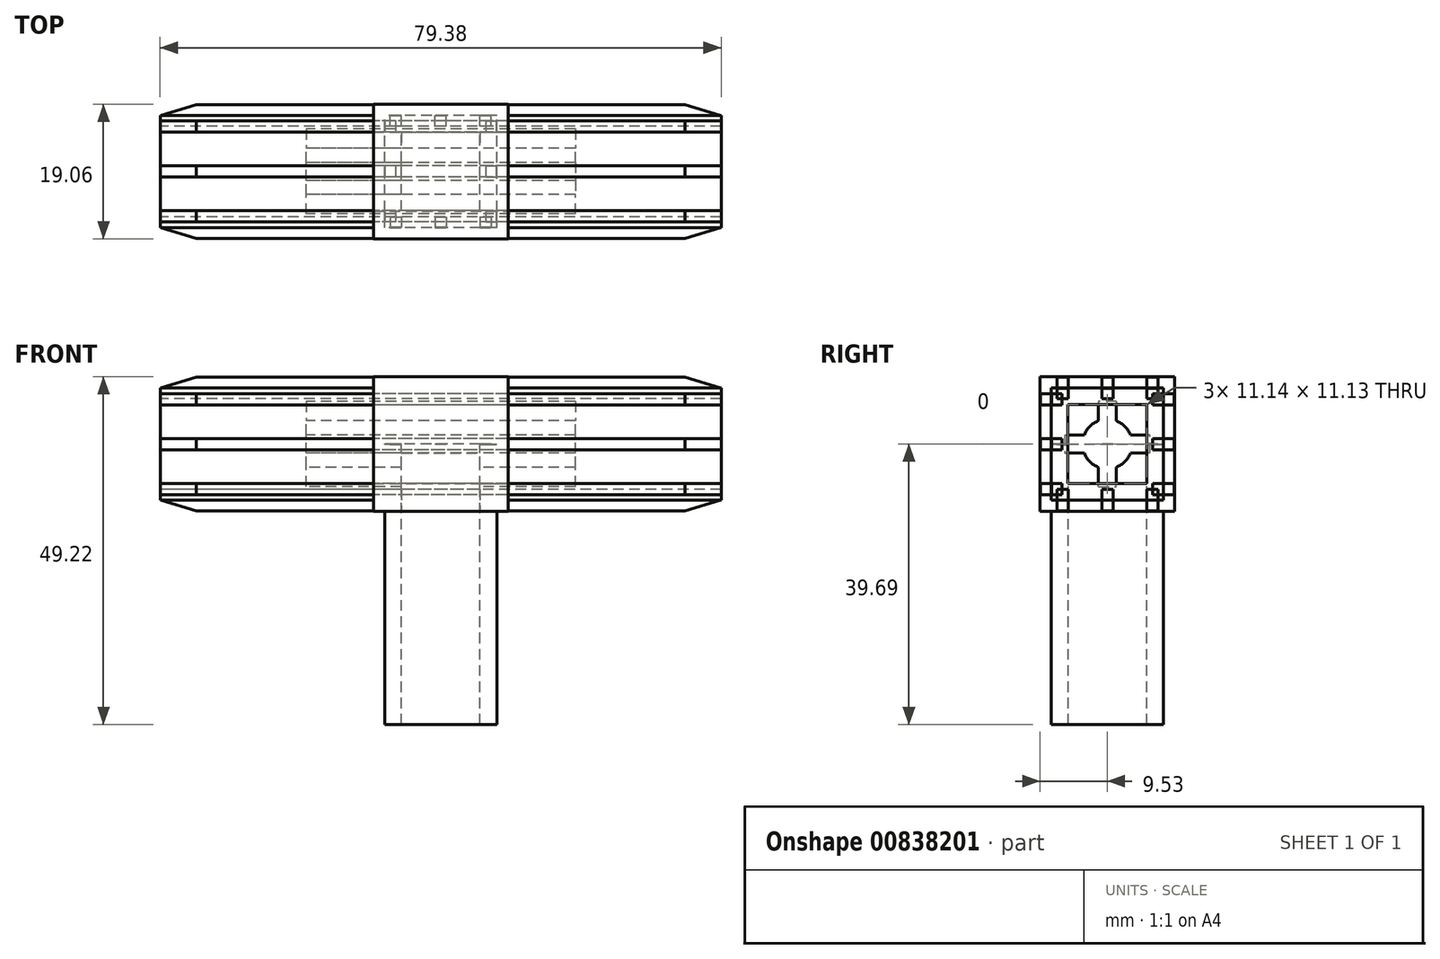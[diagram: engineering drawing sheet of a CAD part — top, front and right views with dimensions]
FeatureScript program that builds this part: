
annotation { "Feature Type Name" : "Feature", "Feature Type Description" : "" }
export const myFeature = defineFeature(function(context is Context, id is Id, definition is map)
    precondition{}
    {
        {
            var Q0;
            Q0=qCreatedBy(makeId("Top.planeOp"),FACE);
            var sketch = newSketch(context, id + "F0", { "sketchPlane" : qUnion([Q0])});
            skLineSegment(sketch, "E0.bottom", {"start": v(39.69, -7.94) * mm, "end": v(-39.69, -7.94) * mm});
            skLineSegment(sketch, "E0.top", {"start": v(39.69, 7.94) * mm, "end": v(-39.69, 7.94) * mm});
            skLineSegment(sketch, "E0.left", {"start": v(39.69, -7.94) * mm, "end": v(39.69, 7.94) * mm});
            skLineSegment(sketch, "E0.right", {"start": v(-39.69, -7.94) * mm, "end": v(-39.69, 7.94) * mm});
            skPoint(sketch, "E0.middle", {"position": v(0, 0) * mm});
            skLineSegment(sketch, "E1.bottom", {"start": v(9.53, -9.52) * mm, "end": v(-9.52, -9.53) * mm});
            skLineSegment(sketch, "E1.top", {"start": v(9.52, 9.53) * mm, "end": v(-9.53, 9.53) * mm});
            skLineSegment(sketch, "E1.left", {"start": v(9.53, -9.52) * mm, "end": v(9.52, 9.53) * mm});
            skLineSegment(sketch, "E1.right", {"start": v(-9.52, -9.53) * mm, "end": v(-9.53, 9.53) * mm});
            skSolve(sketch);
        }
        {
            var Q0;
            {var subQ0=sQuery(id+"F0.wireOp",EDGE,"E0.right");Q0=makeQuery(id+"F0.imprint","IMPRINT",FACE,{"disambiguationData":[TD([[makeQuery(id+"F0.imprint","IMPRINT",EDGE,{"derivedFrom":subQ0}),-1.0]])]});}
            var Q1;
            {var subQ0=sQuery(id+"F0.wireOp",EDGE,"E0.left");Q1=makeQuery(id+"F0.imprint","IMPRINT",FACE,{"disambiguationData":[TD([[makeQuery(id+"F0.imprint","IMPRINT",EDGE,{"derivedFrom":subQ0}),1.0]])]});}
            extrude(context, id + "F1", {"entities" : qUnion([Q0, Q1]), "endBound" : BoundingType.SYMMETRIC, "depth" : 15.88 * mm, "offsetDistance" : 25.4 * mm});
        }
        {
            var Q0;
            {var subQ0=sQuery(id+"F0.wireOp",EDGE,"E1.left");var subQ1=sQuery(id+"F0.wireOp",EDGE,"E0.bottom");var subQ2=makeQuery(id+"F0.imprint","INTERSECT",VERTEX,{"derivedFrom":[subQ1,subQ0]});Q0=makeQuery(id+"F0.imprint","IMPRINT",FACE,{"disambiguationData":[TD([[makeQuery(id+"F0.imprint","IMPRINT",EDGE,{"disambiguationData":[TD([[subQ2,-1.0]])],"derivedFrom":subQ1}),-1.0]])]});}
            var Q1;
            {var subQ5=sQuery(id+"F0.wireOp",EDGE,"E1.top");Q1=makeQuery(id+"F0.imprint","IMPRINT",FACE,{"disambiguationData":[TD([[makeQuery(id+"F0.imprint","IMPRINT",EDGE,{"derivedFrom":subQ5}),1.0]])]});}
            var Q2;
            {var subQ5=sQuery(id+"F0.wireOp",EDGE,"E1.bottom");Q2=makeQuery(id+"F0.imprint","IMPRINT",FACE,{"disambiguationData":[TD([[makeQuery(id+"F0.imprint","IMPRINT",EDGE,{"derivedFrom":subQ5}),-1.0]])]});}
            extrude(context, id + "F2", {"entities" : qUnion([Q0, Q1, Q2]), "endBound" : BoundingType.SYMMETRIC, "depth" : 19.05 * mm, "offsetDistance" : 25.4 * mm});
        }
        {
            var Q0;
            Q0=qCreatedBy(makeId("Right.planeOp"),FACE);
            var sketch = newSketch(context, id + "F3", { "sketchPlane" : qUnion([Q0])});
            skLineSegment(sketch, "E2.bottom", {"start": v(5.57, -5.56) * mm, "end": v(-5.57, -5.56) * mm});
            skLineSegment(sketch, "E2.top", {"start": v(5.57, 5.56) * mm, "end": v(-5.57, 5.56) * mm});
            skLineSegment(sketch, "E2.left", {"start": v(5.57, -5.56) * mm, "end": v(5.57, 5.56) * mm});
            skLineSegment(sketch, "E2.right", {"start": v(-5.57, -5.56) * mm, "end": v(-5.57, 5.56) * mm});
            skPoint(sketch, "E2.middle", {"position": v(0, 0) * mm});
            skLineSegment(sketch, "E3", {"start": v(-7.94, 7.94) * mm, "end": v(7.94, 7.94) * mm});
            skLineSegment(sketch, "E4.bottom", {"start": v(0.8, 6.41) * mm, "end": v(-0.8, 6.41) * mm});
            skLineSegment(sketch, "E4.top", {"start": v(0.8, 9.46) * mm, "end": v(-0.8, 9.46) * mm});
            skLineSegment(sketch, "E4.left", {"start": v(0.8, 6.41) * mm, "end": v(0.8, 9.46) * mm});
            skLineSegment(sketch, "E4.right", {"start": v(-0.8, 6.41) * mm, "end": v(-0.8, 9.46) * mm});
            skPoint(sketch, "E4.middle", {"position": v(0, 7.94) * mm});
            skLineSegment(sketch, "E5.bottom", {"start": v(-5.56, 6.41) * mm, "end": v(-7.14, 6.41) * mm});
            skLineSegment(sketch, "E5.top", {"start": v(-5.56, 9.46) * mm, "end": v(-7.14, 9.46) * mm});
            skLineSegment(sketch, "E5.left", {"start": v(-5.56, 6.41) * mm, "end": v(-5.56, 9.46) * mm});
            skLineSegment(sketch, "E5.right", {"start": v(-7.14, 6.41) * mm, "end": v(-7.14, 9.46) * mm});
            skPoint(sketch, "E5.middle", {"position": v(-6.35, 7.94) * mm});
            skLineSegment(sketch, "E6.bottom", {"start": v(7.14, 6.41) * mm, "end": v(5.56, 6.41) * mm});
            skLineSegment(sketch, "E6.top", {"start": v(7.14, 9.46) * mm, "end": v(5.56, 9.46) * mm});
            skLineSegment(sketch, "E6.left", {"start": v(7.14, 6.41) * mm, "end": v(7.14, 9.46) * mm});
            skLineSegment(sketch, "E6.right", {"start": v(5.56, 6.41) * mm, "end": v(5.56, 9.46) * mm});
            skPoint(sketch, "E6.middle", {"position": v(6.35, 7.94) * mm});
            skLineSegment(sketch, "E7.1.0", {"start": v(-6.41, -7.14) * mm, "end": v(-9.46, -7.14) * mm});
            skLineSegment(sketch, "E7.1.1", {"start": v(-9.46, -5.56) * mm, "end": v(-9.46, -7.14) * mm});
            skLineSegment(sketch, "E7.1.2", {"start": v(-6.41, -5.56) * mm, "end": v(-9.46, -5.56) * mm});
            skLineSegment(sketch, "E7.1.3", {"start": v(-6.41, -5.56) * mm, "end": v(-6.41, -7.14) * mm});
            skLineSegment(sketch, "E7.1.4", {"start": v(-6.41, -0.8) * mm, "end": v(-9.46, -0.8) * mm});
            skLineSegment(sketch, "E7.1.5", {"start": v(-6.41, 0.8) * mm, "end": v(-6.41, -0.8) * mm});
            skLineSegment(sketch, "E7.1.6", {"start": v(-6.41, 0.8) * mm, "end": v(-9.46, 0.8) * mm});
            skLineSegment(sketch, "E7.1.7", {"start": v(-9.46, 0.8) * mm, "end": v(-9.46, -0.8) * mm});
            skLineSegment(sketch, "E7.1.8", {"start": v(-6.41, 5.56) * mm, "end": v(-9.46, 5.56) * mm});
            skLineSegment(sketch, "E7.1.9", {"start": v(-6.41, 7.14) * mm, "end": v(-9.46, 7.14) * mm});
            skLineSegment(sketch, "E7.1.10", {"start": v(-6.41, 7.14) * mm, "end": v(-6.41, 5.56) * mm});
            skLineSegment(sketch, "E7.1.11", {"start": v(-9.46, 7.14) * mm, "end": v(-9.46, 5.56) * mm});
            skLineSegment(sketch, "E7.2.0", {"start": v(7.14, -6.41) * mm, "end": v(7.14, -9.46) * mm});
            skLineSegment(sketch, "E7.2.1", {"start": v(5.56, -9.46) * mm, "end": v(7.14, -9.46) * mm});
            skLineSegment(sketch, "E7.2.2", {"start": v(5.56, -6.41) * mm, "end": v(5.56, -9.46) * mm});
            skLineSegment(sketch, "E7.2.3", {"start": v(5.56, -6.41) * mm, "end": v(7.14, -6.41) * mm});
            skLineSegment(sketch, "E7.2.4", {"start": v(0.8, -6.41) * mm, "end": v(0.8, -9.46) * mm});
            skLineSegment(sketch, "E7.2.5", {"start": v(-0.8, -6.41) * mm, "end": v(0.8, -6.41) * mm});
            skLineSegment(sketch, "E7.2.6", {"start": v(-0.8, -6.41) * mm, "end": v(-0.8, -9.46) * mm});
            skLineSegment(sketch, "E7.2.7", {"start": v(-0.8, -9.46) * mm, "end": v(0.8, -9.46) * mm});
            skLineSegment(sketch, "E7.2.8", {"start": v(-5.56, -6.41) * mm, "end": v(-5.56, -9.46) * mm});
            skLineSegment(sketch, "E7.2.9", {"start": v(-7.14, -6.41) * mm, "end": v(-7.14, -9.46) * mm});
            skLineSegment(sketch, "E7.2.10", {"start": v(-7.14, -6.41) * mm, "end": v(-5.56, -6.41) * mm});
            skLineSegment(sketch, "E7.2.11", {"start": v(-7.14, -9.46) * mm, "end": v(-5.56, -9.46) * mm});
            skLineSegment(sketch, "E8.1.3.0", {"start": v(6.41, 7.14) * mm, "end": v(9.46, 7.14) * mm});
            skLineSegment(sketch, "E8.3.3.0", {"start": v(9.46, 5.56) * mm, "end": v(9.46, 7.14) * mm});
            skLineSegment(sketch, "E8.6.3.0", {"start": v(6.41, 5.56) * mm, "end": v(9.46, 5.56) * mm});
            skLineSegment(sketch, "E8.9.3.0", {"start": v(6.41, 5.56) * mm, "end": v(6.41, 7.14) * mm});
            skLineSegment(sketch, "E8.12.3.0", {"start": v(6.41, 0.8) * mm, "end": v(9.46, 0.8) * mm});
            skLineSegment(sketch, "E8.15.3.0", {"start": v(6.41, -0.8) * mm, "end": v(6.41, 0.8) * mm});
            skLineSegment(sketch, "E8.18.3.0", {"start": v(6.41, -0.8) * mm, "end": v(9.46, -0.8) * mm});
            skLineSegment(sketch, "E8.21.3.0", {"start": v(9.46, -0.8) * mm, "end": v(9.46, 0.8) * mm});
            skLineSegment(sketch, "E8.24.3.0", {"start": v(6.41, -5.56) * mm, "end": v(9.46, -5.56) * mm});
            skLineSegment(sketch, "E8.27.3.0", {"start": v(6.41, -7.14) * mm, "end": v(9.46, -7.14) * mm});
            skLineSegment(sketch, "E8.30.3.0", {"start": v(6.41, -7.14) * mm, "end": v(6.41, -5.56) * mm});
            skLineSegment(sketch, "E8.33.3.0", {"start": v(9.46, -7.14) * mm, "end": v(9.46, -5.56) * mm});
            skSolve(sketch);
        }
        {
            var Q0;
            Q0=makeQuery(id+"F3.imprint","IMPRINT",FACE,{"disambiguationData":[TD([[makeQuery(id+"F3.imprint","IMPRINT",EDGE,{"derivedFrom":sQuery(id+"F3.wireOp",EDGE,"E7.1.4")}),-1.0]])]});
            var Q1;
            {var subQ6=sQuery(id+"F3.wireOp",EDGE,"E7.1.8");Q1=makeQuery(id+"F3.imprint","IMPRINT",FACE,{"disambiguationData":[TD([[makeQuery(id+"F3.imprint","IMPRINT",EDGE,{"derivedFrom":subQ6}),-1.0]])]});}
            var Q2;
            {var subQ5=sQuery(id+"F3.wireOp",EDGE,"E5.top");Q2=makeQuery(id+"F3.imprint","IMPRINT",FACE,{"disambiguationData":[TD([[makeQuery(id+"F3.imprint","IMPRINT",EDGE,{"derivedFrom":subQ5}),1.0]])]});}
            var Q3;
            {var subQ0=sQuery(id+"F3.wireOp",EDGE,"E5.left");var subQ3=sQuery(id+"F3.wireOp",EDGE,"E3");var subQ4=makeQuery(id+"F3.imprint","INTERSECT",VERTEX,{"derivedFrom":[subQ3,subQ0]});Q3=makeQuery(id+"F3.imprint","IMPRINT",FACE,{"disambiguationData":[TD([[makeQuery(id+"F3.imprint","IMPRINT",EDGE,{"disambiguationData":[TD([[subQ4,1.0]])],"derivedFrom":subQ3}),-1.0]])]});}
            var Q4;
            {var subQ5=sQuery(id+"F3.wireOp",EDGE,"E4.bottom");Q4=makeQuery(id+"F3.imprint","IMPRINT",FACE,{"disambiguationData":[TD([[makeQuery(id+"F3.imprint","IMPRINT",EDGE,{"derivedFrom":subQ5}),-1.0]])]});}
            var Q5;
            {var subQ5=sQuery(id+"F3.wireOp",EDGE,"E4.top");Q5=makeQuery(id+"F3.imprint","IMPRINT",FACE,{"disambiguationData":[TD([[makeQuery(id+"F3.imprint","IMPRINT",EDGE,{"derivedFrom":subQ5}),1.0]])]});}
            var Q6;
            {var subQ5=sQuery(id+"F3.wireOp",EDGE,"E6.top");Q6=makeQuery(id+"F3.imprint","IMPRINT",FACE,{"disambiguationData":[TD([[makeQuery(id+"F3.imprint","IMPRINT",EDGE,{"derivedFrom":subQ5}),1.0]])]});}
            var Q7;
            {var subQ0=sQuery(id+"F3.wireOp",EDGE,"E6.left");var subQ1=sQuery(id+"F3.wireOp",EDGE,"E3");var subQ2=makeQuery(id+"F3.imprint","INTERSECT",VERTEX,{"derivedFrom":[subQ1,subQ0]});Q7=makeQuery(id+"F3.imprint","IMPRINT",FACE,{"disambiguationData":[TD([[makeQuery(id+"F3.imprint","IMPRINT",EDGE,{"disambiguationData":[TD([[subQ2,1.0]])],"derivedFrom":subQ1}),-1.0]])]});}
            var Q8;
            {var subQ0=sQuery(id+"F3.wireOp",EDGE,"E8.3.3.0");Q8=makeQuery(id+"F3.imprint","IMPRINT",FACE,{"disambiguationData":[TD([[makeQuery(id+"F3.imprint","IMPRINT",EDGE,{"derivedFrom":subQ0}),1.0]])]});}
            var Q9;
            Q9=makeQuery(id+"F3.imprint","IMPRINT",FACE,{"disambiguationData":[TD([[makeQuery(id+"F3.imprint","IMPRINT",EDGE,{"derivedFrom":sQuery(id+"F3.wireOp",EDGE,"E8.12.3.0")}),-1.0]])]});
            var Q10;
            {var subQ4=sQuery(id+"F3.wireOp",EDGE,"E8.24.3.0");Q10=makeQuery(id+"F3.imprint","IMPRINT",FACE,{"disambiguationData":[TD([[makeQuery(id+"F3.imprint","IMPRINT",EDGE,{"derivedFrom":subQ4}),-1.0]])]});}
            var Q11;
            {var subQ4=sQuery(id+"F3.wireOp",EDGE,"E7.2.1");Q11=makeQuery(id+"F3.imprint","IMPRINT",FACE,{"disambiguationData":[TD([[makeQuery(id+"F3.imprint","IMPRINT",EDGE,{"derivedFrom":subQ4}),1.0]])]});}
            var Q12;
            Q12=makeQuery(id+"F3.imprint","IMPRINT",FACE,{"disambiguationData":[TD([[makeQuery(id+"F3.imprint","IMPRINT",EDGE,{"derivedFrom":sQuery(id+"F3.wireOp",EDGE,"E7.2.4")}),-1.0]])]});
            var Q13;
            {var subQ4=sQuery(id+"F3.wireOp",EDGE,"E7.2.8");Q13=makeQuery(id+"F3.imprint","IMPRINT",FACE,{"disambiguationData":[TD([[makeQuery(id+"F3.imprint","IMPRINT",EDGE,{"derivedFrom":subQ4}),-1.0]])]});}
            var Q14;
            {var subQ4=sQuery(id+"F3.wireOp",EDGE,"E7.1.1");Q14=makeQuery(id+"F3.imprint","IMPRINT",FACE,{"disambiguationData":[TD([[makeQuery(id+"F3.imprint","IMPRINT",EDGE,{"derivedFrom":subQ4}),1.0]])]});}
            extrude(context, id + "F4", {"entities" : qUnion([Q0, Q1, Q2, Q3, Q4, Q5, Q6, Q7, Q8, Q9, Q10, Q11, Q12, Q13, Q14]), "endBound" : BoundingType.SYMMETRIC, "depth" : 79.38 * mm, "offsetDistance" : 25.4 * mm});
        }
        {
            var Q0;
            Q0=makeQuery(id+"F3.imprint","IMPRINT",FACE,{"disambiguationData":[TD([[makeQuery(id+"F3.imprint","IMPRINT",EDGE,{"derivedFrom":sQuery(id+"F3.wireOp",EDGE,"E2.bottom")}),-1.0]])]});
            extrude(context, id + "F5", {"entities" : qUnion([Q0]), "operationType" : NewBodyOperationType.REMOVE, "endBound" : BoundingType.SYMMETRIC, "oppositeDirection" : true, "depth" : 79.38 * mm, "offsetDistance" : 25.4 * mm});
        }
        {
            var Q0;
            Q0=qCreatedBy(makeId("Right.planeOp"),FACE);
            var sketch = newSketch(context, id + "F6", { "sketchPlane" : qUnion([Q0])});
            skCircle(sketch, "E9", {"center": v(0, 0) * mm, "radius": 3.52 * mm});
            skLineSegment(sketch, "E10.bottom", {"start": v(1.27, 6.01) * mm, "end": v(-1.27, 6.01) * mm});
            skLineSegment(sketch, "E10.top", {"start": v(1.27, 1.02) * mm, "end": v(-1.27, 1.02) * mm});
            skLineSegment(sketch, "E10.left", {"start": v(1.27, 6.01) * mm, "end": v(1.27, 1.02) * mm});
            skLineSegment(sketch, "E10.right", {"start": v(-1.27, 6.01) * mm, "end": v(-1.27, 1.02) * mm});
            skPoint(sketch, "E10.middle", {"position": v(0, 3.52) * mm});
            skLineSegment(sketch, "E11.1.0", {"start": v(-6.01, -1.27) * mm, "end": v(-1.02, -1.27) * mm});
            skLineSegment(sketch, "E11.1.1", {"start": v(-6.01, 1.27) * mm, "end": v(-6.01, -1.27) * mm});
            skLineSegment(sketch, "E11.1.2", {"start": v(-6.01, 1.27) * mm, "end": v(-1.02, 1.27) * mm});
            skLineSegment(sketch, "E11.1.3", {"start": v(-1.02, 1.27) * mm, "end": v(-1.02, -1.27) * mm});
            skLineSegment(sketch, "E11.2.0", {"start": v(1.27, -6.01) * mm, "end": v(1.27, -1.02) * mm});
            skLineSegment(sketch, "E11.2.1", {"start": v(-1.27, -6.01) * mm, "end": v(1.27, -6.01) * mm});
            skLineSegment(sketch, "E11.2.2", {"start": v(-1.27, -6.01) * mm, "end": v(-1.27, -1.02) * mm});
            skLineSegment(sketch, "E11.2.3", {"start": v(-1.27, -1.02) * mm, "end": v(1.27, -1.02) * mm});
            skLineSegment(sketch, "E12.2.3.0", {"start": v(6.01, 1.27) * mm, "end": v(1.02, 1.27) * mm});
            skLineSegment(sketch, "E12.3.3.0", {"start": v(6.01, -1.27) * mm, "end": v(6.01, 1.27) * mm});
            skLineSegment(sketch, "E12.6.3.0", {"start": v(6.01, -1.27) * mm, "end": v(1.02, -1.27) * mm});
            skLineSegment(sketch, "E12.9.3.0", {"start": v(1.02, -1.27) * mm, "end": v(1.02, 1.27) * mm});
            skSolve(sketch);
        }
        {
            var Q0;
            {var subQ0=sQuery(id+"F6.wireOp",EDGE,"E10.right");var subQ1=sQuery(id+"F6.wireOp",EDGE,"E10.top");var subQ2=makeQuery(id+"F6.imprint","INTERSECT",VERTEX,{"derivedFrom":[subQ1,subQ0]});Q0=makeQuery(id+"F6.imprint","IMPRINT",FACE,{"disambiguationData":[TD([[makeQuery(id+"F6.imprint","IMPRINT",EDGE,{"disambiguationData":[TD([[subQ2,1.0]])],"derivedFrom":subQ1}),-1.0]])]});}
            var Q1;
            {var subQ0=sQuery(id+"F6.wireOp",EDGE,"E10.left");var subQ1=sQuery(id+"F6.wireOp",EDGE,"E10.top");var subQ2=makeQuery(id+"F6.imprint","INTERSECT",VERTEX,{"derivedFrom":[subQ1,subQ0]});Q1=makeQuery(id+"F6.imprint","IMPRINT",FACE,{"disambiguationData":[TD([[makeQuery(id+"F6.imprint","IMPRINT",EDGE,{"disambiguationData":[TD([[subQ2,-1.0]])],"derivedFrom":subQ1}),-1.0]])]});}
            var Q2;
            {var subQ0=sQuery(id+"F6.wireOp",EDGE,"E11.2.3");var subQ1=sQuery(id+"F6.wireOp",EDGE,"E11.2.0");var subQ2=makeQuery(id+"F6.imprint","INTERSECT",VERTEX,{"derivedFrom":[subQ1,subQ0]});Q2=makeQuery(id+"F6.imprint","IMPRINT",FACE,{"disambiguationData":[TD([[makeQuery(id+"F6.imprint","IMPRINT",EDGE,{"disambiguationData":[TD([[subQ2,1.0]])],"derivedFrom":subQ1}),1.0]])]});}
            var Q3;
            {var subQ0=sQuery(id+"F6.wireOp",EDGE,"E11.1.3");var subQ1=sQuery(id+"F6.wireOp",EDGE,"E11.1.0");var subQ2=makeQuery(id+"F6.imprint","INTERSECT",VERTEX,{"derivedFrom":[subQ1,subQ0]});Q3=makeQuery(id+"F6.imprint","IMPRINT",FACE,{"disambiguationData":[TD([[makeQuery(id+"F6.imprint","IMPRINT",EDGE,{"disambiguationData":[TD([[subQ2,1.0]])],"derivedFrom":subQ1}),1.0]])]});}
            var Q4;
            {var subQ0=sQuery(id+"F6.wireOp",EDGE,"E12.9.3.0");var subQ1=sQuery(id+"F6.wireOp",EDGE,"E10.top");var subQ2=makeQuery(id+"F6.imprint","INTERSECT",VERTEX,{"derivedFrom":[subQ1,subQ0]});Q4=makeQuery(id+"F6.imprint","IMPRINT",FACE,{"disambiguationData":[TD([[makeQuery(id+"F6.imprint","IMPRINT",EDGE,{"disambiguationData":[TD([[subQ2,-1.0]])],"derivedFrom":subQ1}),1.0]])]});}
            var Q5;
            {var subQ8=sQuery(id+"F6.wireOp",EDGE,"E12.2.3.0");var subQ12=sQuery(id+"F6.wireOp",EDGE,"E9");var subQ13=makeQuery(id+"F6.imprint","INTERSECT",VERTEX,{"derivedFrom":[subQ12,subQ8]});Q5=makeQuery(id+"F6.imprint","IMPRINT",FACE,{"disambiguationData":[TD([[makeQuery(id+"F6.imprint","IMPRINT",EDGE,{"disambiguationData":[TD([[subQ13,1.0]])],"derivedFrom":subQ12}),1.0]])]});}
            var Q6;
            {var subQ0=sQuery(id+"F6.wireOp",EDGE,"E10.left");var subQ1=sQuery(id+"F6.wireOp",EDGE,"E9");var subQ2=makeQuery(id+"F6.imprint","INTERSECT",VERTEX,{"derivedFrom":[subQ1,subQ0]});Q6=makeQuery(id+"F6.imprint","IMPRINT",FACE,{"disambiguationData":[TD([[makeQuery(id+"F6.imprint","IMPRINT",EDGE,{"disambiguationData":[TD([[subQ2,-1.0]])],"derivedFrom":subQ1}),1.0]])]});}
            var Q7;
            {var subQ1=sQuery(id+"F6.wireOp",EDGE,"E9");var subQ8=sQuery(id+"F6.wireOp",EDGE,"E11.1.2");var subQ12=makeQuery(id+"F6.imprint","INTERSECT",VERTEX,{"derivedFrom":[subQ1,subQ8]});Q7=makeQuery(id+"F6.imprint","IMPRINT",FACE,{"disambiguationData":[TD([[makeQuery(id+"F6.imprint","IMPRINT",EDGE,{"disambiguationData":[TD([[subQ12,-1.0]])],"derivedFrom":subQ1}),1.0]])]});}
            var Q8;
            {var subQ1=sQuery(id+"F6.wireOp",EDGE,"E9");var subQ10=sQuery(id+"F6.wireOp",EDGE,"E11.2.2");var subQ11=makeQuery(id+"F6.imprint","INTERSECT",VERTEX,{"derivedFrom":[subQ1,subQ10]});Q8=makeQuery(id+"F6.imprint","IMPRINT",FACE,{"disambiguationData":[TD([[makeQuery(id+"F6.imprint","IMPRINT",EDGE,{"disambiguationData":[TD([[subQ11,-1.0]])],"derivedFrom":subQ1}),1.0]])]});}
            var Q9;
            {var subQ0=sQuery(id+"F6.wireOp",EDGE,"E11.2.0");var subQ1=sQuery(id+"F6.wireOp",EDGE,"E9");var subQ2=makeQuery(id+"F6.imprint","INTERSECT",VERTEX,{"derivedFrom":[subQ1,subQ0]});Q9=makeQuery(id+"F6.imprint","IMPRINT",FACE,{"disambiguationData":[TD([[makeQuery(id+"F6.imprint","IMPRINT",EDGE,{"disambiguationData":[TD([[subQ2,-1.0]])],"derivedFrom":subQ1}),1.0]])]});}
            var Q10;
            {var subQ5=sQuery(id+"F6.wireOp",EDGE,"E11.2.1");Q10=makeQuery(id+"F6.imprint","IMPRINT",FACE,{"disambiguationData":[TD([[makeQuery(id+"F6.imprint","IMPRINT",EDGE,{"derivedFrom":subQ5}),1.0]])]});}
            var Q11;
            {var subQ0=sQuery(id+"F6.wireOp",EDGE,"E11.1.0");var subQ1=sQuery(id+"F6.wireOp",EDGE,"E9");var subQ2=makeQuery(id+"F6.imprint","INTERSECT",VERTEX,{"derivedFrom":[subQ1,subQ0]});Q11=makeQuery(id+"F6.imprint","IMPRINT",FACE,{"disambiguationData":[TD([[makeQuery(id+"F6.imprint","IMPRINT",EDGE,{"disambiguationData":[TD([[subQ2,-1.0]])],"derivedFrom":subQ1}),1.0]])]});}
            var Q12;
            {var subQ5=sQuery(id+"F6.wireOp",EDGE,"E11.1.1");Q12=makeQuery(id+"F6.imprint","IMPRINT",FACE,{"disambiguationData":[TD([[makeQuery(id+"F6.imprint","IMPRINT",EDGE,{"derivedFrom":subQ5}),1.0]])]});}
            var Q13;
            {var subQ0=sQuery(id+"F6.wireOp",EDGE,"E10.right");var subQ1=sQuery(id+"F6.wireOp",EDGE,"E9");var subQ2=makeQuery(id+"F6.imprint","INTERSECT",VERTEX,{"derivedFrom":[subQ1,subQ0]});Q13=makeQuery(id+"F6.imprint","IMPRINT",FACE,{"disambiguationData":[TD([[makeQuery(id+"F6.imprint","IMPRINT",EDGE,{"disambiguationData":[TD([[subQ2,-1.0]])],"derivedFrom":subQ1}),1.0]])]});}
            var Q14;
            {var subQ0=sQuery(id+"F6.wireOp",EDGE,"E10.left");var subQ1=sQuery(id+"F6.wireOp",EDGE,"E9");var subQ2=makeQuery(id+"F6.imprint","INTERSECT",VERTEX,{"derivedFrom":[subQ1,subQ0]});Q14=makeQuery(id+"F6.imprint","IMPRINT",FACE,{"disambiguationData":[TD([[makeQuery(id+"F6.imprint","IMPRINT",EDGE,{"disambiguationData":[TD([[subQ2,1.0]])],"derivedFrom":subQ1}),1.0]])]});}
            var Q15;
            {var subQ5=sQuery(id+"F6.wireOp",EDGE,"E12.3.3.0");Q15=makeQuery(id+"F6.imprint","IMPRINT",FACE,{"disambiguationData":[TD([[makeQuery(id+"F6.imprint","IMPRINT",EDGE,{"derivedFrom":subQ5}),1.0]])]});}
            var Q16;
            {var subQ5=sQuery(id+"F6.wireOp",EDGE,"E10.bottom");Q16=makeQuery(id+"F6.imprint","IMPRINT",FACE,{"disambiguationData":[TD([[makeQuery(id+"F6.imprint","IMPRINT",EDGE,{"derivedFrom":subQ5}),1.0]])]});}
            extrude(context, id + "F7", {"entities" : qUnion([Q0, Q1, Q2, Q3, Q4, Q5, Q6, Q7, Q8, Q9, Q10, Q11, Q12, Q13, Q14, Q15, Q16]), "endBound" : BoundingType.SYMMETRIC, "depth" : 38.1 * mm, "offsetDistance" : 25.4 * mm});
        }
        {
            var Q0;
            Q0=makeQuery(id+"F4.opExtrude","CAP_EDGE",EDGE,{"disambiguationData":[OSD([sQuery(id+"F3.wireOp",EDGE,"E6.top")])],"isStart":true});
            var Q1;
            Q1=makeQuery(id+"F4.opExtrude","CAP_EDGE",EDGE,{"disambiguationData":[OSD([sQuery(id+"F3.wireOp",EDGE,"E4.top")])],"isStart":true});
            var Q2;
            Q2=makeQuery(id+"F4.opExtrude","CAP_EDGE",EDGE,{"disambiguationData":[OSD([sQuery(id+"F3.wireOp",EDGE,"E5.top")])],"isStart":true});
            var Q3;
            Q3=makeQuery(id+"F4.opExtrude","CAP_EDGE",EDGE,{"disambiguationData":[OSD([sQuery(id+"F3.wireOp",EDGE,"E7.1.11")])],"isStart":true});
            var Q4;
            Q4=makeQuery(id+"F4.opExtrude","CAP_EDGE",EDGE,{"disambiguationData":[OSD([sQuery(id+"F3.wireOp",EDGE,"E7.1.7")])],"isStart":true});
            var Q5;
            Q5=makeQuery(id+"F4.opExtrude","CAP_EDGE",EDGE,{"disambiguationData":[OSD([sQuery(id+"F3.wireOp",EDGE,"E7.1.1")])],"isStart":true});
            var Q6;
            Q6=makeQuery(id+"F4.opExtrude","CAP_EDGE",EDGE,{"disambiguationData":[OSD([sQuery(id+"F3.wireOp",EDGE,"E7.2.11")])],"isStart":true});
            var Q7;
            Q7=makeQuery(id+"F4.opExtrude","CAP_EDGE",EDGE,{"disambiguationData":[OSD([sQuery(id+"F3.wireOp",EDGE,"E7.2.7")])],"isStart":true});
            var Q8;
            Q8=makeQuery(id+"F4.opExtrude","CAP_EDGE",EDGE,{"disambiguationData":[OSD([sQuery(id+"F3.wireOp",EDGE,"E7.2.1")])],"isStart":true});
            var Q9;
            Q9=makeQuery(id+"F4.opExtrude","CAP_EDGE",EDGE,{"disambiguationData":[OSD([sQuery(id+"F3.wireOp",EDGE,"E8.33.3.0")])],"isStart":true});
            var Q10;
            Q10=makeQuery(id+"F4.opExtrude","CAP_EDGE",EDGE,{"disambiguationData":[OSD([sQuery(id+"F3.wireOp",EDGE,"E8.21.3.0")])],"isStart":true});
            var Q11;
            Q11=makeQuery(id+"F4.opExtrude","CAP_EDGE",EDGE,{"disambiguationData":[OSD([sQuery(id+"F3.wireOp",EDGE,"E8.3.3.0")])],"isStart":true});
            var Q12;
            Q12=makeQuery(id+"F4.opExtrude","CAP_EDGE",EDGE,{"disambiguationData":[OSD([sQuery(id+"F3.wireOp",EDGE,"E5.top")])],"isStart":false});
            var Q13;
            Q13=makeQuery(id+"F4.opExtrude","CAP_EDGE",EDGE,{"disambiguationData":[OSD([sQuery(id+"F3.wireOp",EDGE,"E4.top")])],"isStart":false});
            var Q14;
            Q14=makeQuery(id+"F4.opExtrude","CAP_EDGE",EDGE,{"disambiguationData":[OSD([sQuery(id+"F3.wireOp",EDGE,"E6.top")])],"isStart":false});
            var Q15;
            Q15=makeQuery(id+"F4.opExtrude","CAP_EDGE",EDGE,{"disambiguationData":[OSD([sQuery(id+"F3.wireOp",EDGE,"E8.3.3.0")])],"isStart":false});
            var Q16;
            Q16=makeQuery(id+"F4.opExtrude","CAP_EDGE",EDGE,{"disambiguationData":[OSD([sQuery(id+"F3.wireOp",EDGE,"E8.21.3.0")])],"isStart":false});
            var Q17;
            Q17=makeQuery(id+"F4.opExtrude","CAP_EDGE",EDGE,{"disambiguationData":[OSD([sQuery(id+"F3.wireOp",EDGE,"E8.33.3.0")])],"isStart":false});
            var Q18;
            Q18=makeQuery(id+"F4.opExtrude","CAP_EDGE",EDGE,{"disambiguationData":[OSD([sQuery(id+"F3.wireOp",EDGE,"E7.2.1")])],"isStart":false});
            var Q19;
            Q19=makeQuery(id+"F4.opExtrude","CAP_EDGE",EDGE,{"disambiguationData":[OSD([sQuery(id+"F3.wireOp",EDGE,"E7.2.7")])],"isStart":false});
            var Q20;
            Q20=makeQuery(id+"F4.opExtrude","CAP_EDGE",EDGE,{"disambiguationData":[OSD([sQuery(id+"F3.wireOp",EDGE,"E7.2.11")])],"isStart":false});
            var Q21;
            Q21=makeQuery(id+"F4.opExtrude","CAP_EDGE",EDGE,{"disambiguationData":[OSD([sQuery(id+"F3.wireOp",EDGE,"E7.1.1")])],"isStart":false});
            var Q22;
            Q22=makeQuery(id+"F4.opExtrude","CAP_EDGE",EDGE,{"disambiguationData":[OSD([sQuery(id+"F3.wireOp",EDGE,"E7.1.7")])],"isStart":false});
            var Q23;
            Q23=makeQuery(id+"F4.opExtrude","CAP_EDGE",EDGE,{"disambiguationData":[OSD([sQuery(id+"F3.wireOp",EDGE,"E7.1.11")])],"isStart":false});
            chamfer(context, id + "F8", {"entities" : qUnion([Q0, Q1, Q2, Q3, Q4, Q5, Q6, Q7, Q8, Q9, Q10, Q11, Q12, Q13, Q14, Q15, Q16, Q17, Q18, Q19, Q20, Q21, Q22, Q23]), "chamferType" : ChamferType.OFFSET_ANGLE, "width" : 5.08 * mm, "oppositeDirection" : false, "angle" : 17 * degree, "tangentPropagation" : true});
        }
        {
            var Q0;
            Q0=qCreatedBy(makeId("Front.planeOp"),FACE);
            var sketch = newSketch(context, id + "F9", { "sketchPlane" : qUnion([Q0])});
            skLineSegment(sketch, "E13.bottom", {"start": v(7.94, 39.69) * mm, "end": v(7.94, -39.69) * mm});
            skLineSegment(sketch, "E13.top", {"start": v(-7.94, 39.69) * mm, "end": v(-7.94, -39.69) * mm});
            skLineSegment(sketch, "E13.left", {"start": v(7.94, 39.69) * mm, "end": v(-7.94, 39.69) * mm});
            skLineSegment(sketch, "E13.right", {"start": v(7.94, -39.69) * mm, "end": v(-7.94, -39.69) * mm});
            skPoint(sketch, "E13.middle", {"position": v(0, 0) * mm});
            skLineSegment(sketch, "E14.bottom", {"start": v(9.52, 9.53) * mm, "end": v(9.52, -9.52) * mm});
            skLineSegment(sketch, "E14.top", {"start": v(-9.53, 9.53) * mm, "end": v(-9.53, -9.52) * mm});
            skLineSegment(sketch, "E14.left", {"start": v(9.52, 9.53) * mm, "end": v(-9.53, 9.53) * mm});
            skLineSegment(sketch, "E14.right", {"start": v(9.52, -9.52) * mm, "end": v(-9.53, -9.52) * mm});
            skSolve(sketch);
        }
        {
            var Q0;
            {var subQ0=sQuery(id+"F9.wireOp",EDGE,"E13.right");Q0=makeQuery(id+"F9.imprint","IMPRINT",FACE,{"disambiguationData":[TD([[makeQuery(id+"F9.imprint","IMPRINT",EDGE,{"derivedFrom":subQ0}),-1.0]])]});}
            extrude(context, id + "F10", {"entities" : qUnion([Q0]), "operationType" : NewBodyOperationType.ADD, "endBound" : BoundingType.SYMMETRIC, "depth" : 15.88 * mm, "offsetDistance" : 25.4 * mm});
        }
        {
            var Q0;
            Q0=qCreatedBy(makeId("Top.planeOp"),FACE);
            var sketch = newSketch(context, id + "F11", { "sketchPlane" : qUnion([Q0])});
            skLineSegment(sketch, "E15.bottom", {"start": v(5.57, -5.56) * mm, "end": v(-5.56, -5.56) * mm});
            skLineSegment(sketch, "E15.top", {"start": v(5.57, 5.57) * mm, "end": v(-5.56, 5.57) * mm});
            skLineSegment(sketch, "E15.left", {"start": v(5.57, -5.56) * mm, "end": v(5.57, 5.57) * mm});
            skLineSegment(sketch, "E15.right", {"start": v(-5.56, -5.56) * mm, "end": v(-5.56, 5.57) * mm});
            skPoint(sketch, "E15.middle", {"position": v(0, 0) * mm});
            skLineSegment(sketch, "E16", {"start": v(-7.93, 7.94) * mm, "end": v(7.94, 7.94) * mm});
            skLineSegment(sketch, "E17.bottom", {"start": v(0.8, 6.42) * mm, "end": v(-0.79, 6.42) * mm});
            skLineSegment(sketch, "E17.top", {"start": v(0.8, 9.47) * mm, "end": v(-0.79, 9.47) * mm});
            skLineSegment(sketch, "E17.left", {"start": v(0.8, 6.42) * mm, "end": v(0.8, 9.47) * mm});
            skLineSegment(sketch, "E17.right", {"start": v(-0.79, 6.42) * mm, "end": v(-0.79, 9.47) * mm});
            skPoint(sketch, "E17.middle", {"position": v(0, 7.94) * mm});
            skLineSegment(sketch, "E18.bottom", {"start": v(-5.55, 6.42) * mm, "end": v(-7.14, 6.42) * mm});
            skLineSegment(sketch, "E18.top", {"start": v(-5.55, 9.47) * mm, "end": v(-7.14, 9.47) * mm});
            skLineSegment(sketch, "E18.left", {"start": v(-5.55, 6.42) * mm, "end": v(-5.55, 9.47) * mm});
            skLineSegment(sketch, "E18.right", {"start": v(-7.14, 6.42) * mm, "end": v(-7.14, 9.47) * mm});
            skPoint(sketch, "E18.middle", {"position": v(-6.34, 7.94) * mm});
            skLineSegment(sketch, "E19.bottom", {"start": v(7.15, 6.42) * mm, "end": v(5.56, 6.42) * mm});
            skLineSegment(sketch, "E19.top", {"start": v(7.15, 9.47) * mm, "end": v(5.56, 9.47) * mm});
            skLineSegment(sketch, "E19.left", {"start": v(7.15, 6.42) * mm, "end": v(7.15, 9.47) * mm});
            skLineSegment(sketch, "E19.right", {"start": v(5.56, 6.42) * mm, "end": v(5.56, 9.47) * mm});
            skPoint(sketch, "E19.middle", {"position": v(6.36, 7.94) * mm});
            skLineSegment(sketch, "E20.1.0", {"start": v(-6.4, -7.14) * mm, "end": v(-9.46, -7.14) * mm});
            skLineSegment(sketch, "E20.1.1", {"start": v(-9.46, -5.55) * mm, "end": v(-9.46, -7.14) * mm});
            skLineSegment(sketch, "E20.1.2", {"start": v(-6.4, -5.55) * mm, "end": v(-9.46, -5.55) * mm});
            skLineSegment(sketch, "E20.1.3", {"start": v(-6.4, -5.55) * mm, "end": v(-6.4, -7.14) * mm});
            skLineSegment(sketch, "E20.1.4", {"start": v(-6.4, -0.79) * mm, "end": v(-9.46, -0.79) * mm});
            skLineSegment(sketch, "E20.1.5", {"start": v(-6.4, 0.8) * mm, "end": v(-6.4, -0.79) * mm});
            skLineSegment(sketch, "E20.1.6", {"start": v(-6.4, 0.8) * mm, "end": v(-9.46, 0.8) * mm});
            skLineSegment(sketch, "E20.1.7", {"start": v(-9.46, 0.8) * mm, "end": v(-9.46, -0.79) * mm});
            skLineSegment(sketch, "E20.1.8", {"start": v(-6.4, 5.56) * mm, "end": v(-9.46, 5.56) * mm});
            skLineSegment(sketch, "E20.1.9", {"start": v(-6.4, 7.15) * mm, "end": v(-9.46, 7.15) * mm});
            skLineSegment(sketch, "E20.1.10", {"start": v(-6.4, 7.15) * mm, "end": v(-6.4, 5.56) * mm});
            skLineSegment(sketch, "E20.1.11", {"start": v(-9.46, 7.15) * mm, "end": v(-9.46, 5.56) * mm});
            skLineSegment(sketch, "E20.2.0", {"start": v(7.15, -6.4) * mm, "end": v(7.15, -9.46) * mm});
            skLineSegment(sketch, "E20.2.1", {"start": v(5.56, -9.46) * mm, "end": v(7.15, -9.46) * mm});
            skLineSegment(sketch, "E20.2.2", {"start": v(5.56, -6.4) * mm, "end": v(5.56, -9.46) * mm});
            skLineSegment(sketch, "E20.2.3", {"start": v(5.56, -6.4) * mm, "end": v(7.15, -6.4) * mm});
            skLineSegment(sketch, "E20.2.4", {"start": v(0.8, -6.4) * mm, "end": v(0.8, -9.46) * mm});
            skLineSegment(sketch, "E20.2.5", {"start": v(-0.79, -6.4) * mm, "end": v(0.8, -6.4) * mm});
            skLineSegment(sketch, "E20.2.6", {"start": v(-0.79, -6.4) * mm, "end": v(-0.79, -9.46) * mm});
            skLineSegment(sketch, "E20.2.7", {"start": v(-0.79, -9.46) * mm, "end": v(0.8, -9.46) * mm});
            skLineSegment(sketch, "E20.2.8", {"start": v(-5.55, -6.4) * mm, "end": v(-5.55, -9.46) * mm});
            skLineSegment(sketch, "E20.2.9", {"start": v(-7.14, -6.4) * mm, "end": v(-7.14, -9.46) * mm});
            skLineSegment(sketch, "E20.2.10", {"start": v(-7.14, -6.4) * mm, "end": v(-5.55, -6.4) * mm});
            skLineSegment(sketch, "E20.2.11", {"start": v(-7.14, -9.46) * mm, "end": v(-5.55, -9.46) * mm});
            skLineSegment(sketch, "E21.1.3.0", {"start": v(6.42, 7.15) * mm, "end": v(9.47, 7.15) * mm});
            skLineSegment(sketch, "E21.3.3.0", {"start": v(9.47, 5.56) * mm, "end": v(9.47, 7.15) * mm});
            skLineSegment(sketch, "E21.6.3.0", {"start": v(6.42, 5.56) * mm, "end": v(9.47, 5.56) * mm});
            skLineSegment(sketch, "E21.9.3.0", {"start": v(6.42, 5.56) * mm, "end": v(6.42, 7.15) * mm});
            skLineSegment(sketch, "E21.12.3.0", {"start": v(6.42, 0.8) * mm, "end": v(9.47, 0.8) * mm});
            skLineSegment(sketch, "E21.15.3.0", {"start": v(6.42, -0.79) * mm, "end": v(6.42, 0.8) * mm});
            skLineSegment(sketch, "E21.18.3.0", {"start": v(6.42, -0.79) * mm, "end": v(9.47, -0.79) * mm});
            skLineSegment(sketch, "E21.21.3.0", {"start": v(9.47, -0.79) * mm, "end": v(9.47, 0.8) * mm});
            skLineSegment(sketch, "E21.24.3.0", {"start": v(6.42, -5.55) * mm, "end": v(9.47, -5.55) * mm});
            skLineSegment(sketch, "E21.27.3.0", {"start": v(6.42, -7.14) * mm, "end": v(9.47, -7.14) * mm});
            skLineSegment(sketch, "E21.30.3.0", {"start": v(6.42, -7.14) * mm, "end": v(6.42, -5.55) * mm});
            skLineSegment(sketch, "E21.33.3.0", {"start": v(9.47, -7.14) * mm, "end": v(9.47, -5.55) * mm});
            skSolve(sketch);
        }
        {
            var Q0;
            Q0=makeQuery(id+"F11.imprint","IMPRINT",FACE,{"disambiguationData":[TD([[makeQuery(id+"F11.imprint","IMPRINT",EDGE,{"derivedFrom":sQuery(id+"F11.wireOp",EDGE,"E15.bottom")}),-1.0]])]});
            extrude(context, id + "F12", {"entities" : qUnion([Q0]), "operationType" : NewBodyOperationType.REMOVE, "oppositeDirection" : true, "depth" : 40.64 * mm, "offsetDistance" : 25.4 * mm});
        }
        {
            var Q0;
            {var subQ4=sQuery(id+"F11.wireOp",EDGE,"E20.2.1");Q0=makeQuery(id+"F11.imprint","IMPRINT",FACE,{"disambiguationData":[TD([[makeQuery(id+"F11.imprint","IMPRINT",EDGE,{"derivedFrom":subQ4}),1.0]])]});}
            var Q1;
            {var subQ4=sQuery(id+"F11.wireOp",EDGE,"E21.24.3.0");Q1=makeQuery(id+"F11.imprint","IMPRINT",FACE,{"disambiguationData":[TD([[makeQuery(id+"F11.imprint","IMPRINT",EDGE,{"derivedFrom":subQ4}),-1.0]])]});}
            var Q2;
            Q2=makeQuery(id+"F11.imprint","IMPRINT",FACE,{"disambiguationData":[TD([[makeQuery(id+"F11.imprint","IMPRINT",EDGE,{"derivedFrom":sQuery(id+"F11.wireOp",EDGE,"E21.12.3.0")}),-1.0]])]});
            var Q3;
            {var subQ0=sQuery(id+"F11.wireOp",EDGE,"E21.3.3.0");Q3=makeQuery(id+"F11.imprint","IMPRINT",FACE,{"disambiguationData":[TD([[makeQuery(id+"F11.imprint","IMPRINT",EDGE,{"derivedFrom":subQ0}),1.0]])]});}
            var Q4;
            {var subQ0=sQuery(id+"F11.wireOp",EDGE,"E19.left");var subQ1=sQuery(id+"F11.wireOp",EDGE,"E16");var subQ2=makeQuery(id+"F11.imprint","INTERSECT",VERTEX,{"derivedFrom":[subQ1,subQ0]});Q4=makeQuery(id+"F11.imprint","IMPRINT",FACE,{"disambiguationData":[TD([[makeQuery(id+"F11.imprint","IMPRINT",EDGE,{"disambiguationData":[TD([[subQ2,1.0]])],"derivedFrom":subQ1}),-1.0]])]});}
            var Q5;
            {var subQ5=sQuery(id+"F11.wireOp",EDGE,"E19.top");Q5=makeQuery(id+"F11.imprint","IMPRINT",FACE,{"disambiguationData":[TD([[makeQuery(id+"F11.imprint","IMPRINT",EDGE,{"derivedFrom":subQ5}),1.0]])]});}
            var Q6;
            {var subQ5=sQuery(id+"F11.wireOp",EDGE,"E17.top");Q6=makeQuery(id+"F11.imprint","IMPRINT",FACE,{"disambiguationData":[TD([[makeQuery(id+"F11.imprint","IMPRINT",EDGE,{"derivedFrom":subQ5}),1.0]])]});}
            var Q7;
            {var subQ5=sQuery(id+"F11.wireOp",EDGE,"E17.bottom");Q7=makeQuery(id+"F11.imprint","IMPRINT",FACE,{"disambiguationData":[TD([[makeQuery(id+"F11.imprint","IMPRINT",EDGE,{"derivedFrom":subQ5}),-1.0]])]});}
            var Q8;
            {var subQ5=sQuery(id+"F11.wireOp",EDGE,"E18.top");Q8=makeQuery(id+"F11.imprint","IMPRINT",FACE,{"disambiguationData":[TD([[makeQuery(id+"F11.imprint","IMPRINT",EDGE,{"derivedFrom":subQ5}),1.0]])]});}
            var Q9;
            {var subQ0=sQuery(id+"F11.wireOp",EDGE,"E18.left");var subQ3=sQuery(id+"F11.wireOp",EDGE,"E16");var subQ4=makeQuery(id+"F11.imprint","INTERSECT",VERTEX,{"derivedFrom":[subQ3,subQ0]});Q9=makeQuery(id+"F11.imprint","IMPRINT",FACE,{"disambiguationData":[TD([[makeQuery(id+"F11.imprint","IMPRINT",EDGE,{"disambiguationData":[TD([[subQ4,1.0]])],"derivedFrom":subQ3}),-1.0]])]});}
            var Q10;
            {var subQ6=sQuery(id+"F11.wireOp",EDGE,"E20.1.8");Q10=makeQuery(id+"F11.imprint","IMPRINT",FACE,{"disambiguationData":[TD([[makeQuery(id+"F11.imprint","IMPRINT",EDGE,{"derivedFrom":subQ6}),-1.0]])]});}
            var Q11;
            Q11=makeQuery(id+"F11.imprint","IMPRINT",FACE,{"disambiguationData":[TD([[makeQuery(id+"F11.imprint","IMPRINT",EDGE,{"derivedFrom":sQuery(id+"F11.wireOp",EDGE,"E20.1.4")}),-1.0]])]});
            var Q12;
            {var subQ4=sQuery(id+"F11.wireOp",EDGE,"E20.1.1");Q12=makeQuery(id+"F11.imprint","IMPRINT",FACE,{"disambiguationData":[TD([[makeQuery(id+"F11.imprint","IMPRINT",EDGE,{"derivedFrom":subQ4}),1.0]])]});}
            var Q13;
            {var subQ4=sQuery(id+"F11.wireOp",EDGE,"E20.2.8");Q13=makeQuery(id+"F11.imprint","IMPRINT",FACE,{"disambiguationData":[TD([[makeQuery(id+"F11.imprint","IMPRINT",EDGE,{"derivedFrom":subQ4}),-1.0]])]});}
            var Q14;
            Q14=makeQuery(id+"F11.imprint","IMPRINT",FACE,{"disambiguationData":[TD([[makeQuery(id+"F11.imprint","IMPRINT",EDGE,{"derivedFrom":sQuery(id+"F11.wireOp",EDGE,"E20.2.4")}),-1.0]])]});
            extrude(context, id + "F13", {"entities" : qUnion([Q0, Q1, Q2, Q3, Q4, Q5, Q6, Q7, Q8, Q9, Q10, Q11, Q12, Q13, Q14]), "oppositeDirection" : true, "depth" : 3.12 / 50.8 * mm, "offsetDistance" : 25.4 * mm});
        }
        {
            var Q0;
            Q0=makeQuery(id+"F13.opExtrude","CAP_EDGE",EDGE,{"disambiguationData":[OSD([sQuery(id+"F11.wireOp",EDGE,"E19.top")])],"isStart":false});
            var Q1;
            Q1=makeQuery(id+"F13.opExtrude","CAP_EDGE",EDGE,{"disambiguationData":[OSD([sQuery(id+"F11.wireOp",EDGE,"E17.top")])],"isStart":false});
            var Q2;
            Q2=makeQuery(id+"F13.opExtrude","CAP_EDGE",EDGE,{"disambiguationData":[OSD([sQuery(id+"F11.wireOp",EDGE,"E18.top")])],"isStart":false});
            var Q3;
            Q3=makeQuery(id+"F13.opExtrude","CAP_EDGE",EDGE,{"disambiguationData":[OSD([sQuery(id+"F11.wireOp",EDGE,"E20.1.11")])],"isStart":false});
            var Q4;
            Q4=makeQuery(id+"F13.opExtrude","CAP_EDGE",EDGE,{"disambiguationData":[OSD([sQuery(id+"F11.wireOp",EDGE,"E20.1.7")])],"isStart":false});
            var Q5;
            Q5=makeQuery(id+"F13.opExtrude","CAP_EDGE",EDGE,{"disambiguationData":[OSD([sQuery(id+"F11.wireOp",EDGE,"E21.21.3.0")])],"isStart":false});
            var Q6;
            Q6=makeQuery(id+"F13.opExtrude","CAP_EDGE",EDGE,{"disambiguationData":[OSD([sQuery(id+"F11.wireOp",EDGE,"E21.33.3.0")])],"isStart":false});
            var Q7;
            Q7=makeQuery(id+"F13.opExtrude","CAP_EDGE",EDGE,{"disambiguationData":[OSD([sQuery(id+"F11.wireOp",EDGE,"E21.3.3.0")])],"isStart":false});
            var Q8;
            Q8=makeQuery(id+"F13.opExtrude","CAP_EDGE",EDGE,{"disambiguationData":[OSD([sQuery(id+"F11.wireOp",EDGE,"E20.2.1")])],"isStart":false});
            var Q9;
            Q9=makeQuery(id+"F13.opExtrude","CAP_EDGE",EDGE,{"disambiguationData":[OSD([sQuery(id+"F11.wireOp",EDGE,"E20.2.7")])],"isStart":false});
            var Q10;
            Q10=makeQuery(id+"F13.opExtrude","CAP_EDGE",EDGE,{"disambiguationData":[OSD([sQuery(id+"F11.wireOp",EDGE,"E20.2.11")])],"isStart":false});
            var Q11;
            Q11=makeQuery(id+"F13.opExtrude","CAP_EDGE",EDGE,{"disambiguationData":[OSD([sQuery(id+"F11.wireOp",EDGE,"E20.1.1")])],"isStart":false});
            chamfer(context, id + "F14", {"entities" : qUnion([Q0, Q1, Q2, Q3, Q4, Q5, Q6, Q7, Q8, Q9, Q10, Q11]), "chamferType" : ChamferType.OFFSET_ANGLE, "width" : 5.08 * mm, "oppositeDirection" : false, "angle" : 17 * degree, "tangentPropagation" : true});
        }
    });
